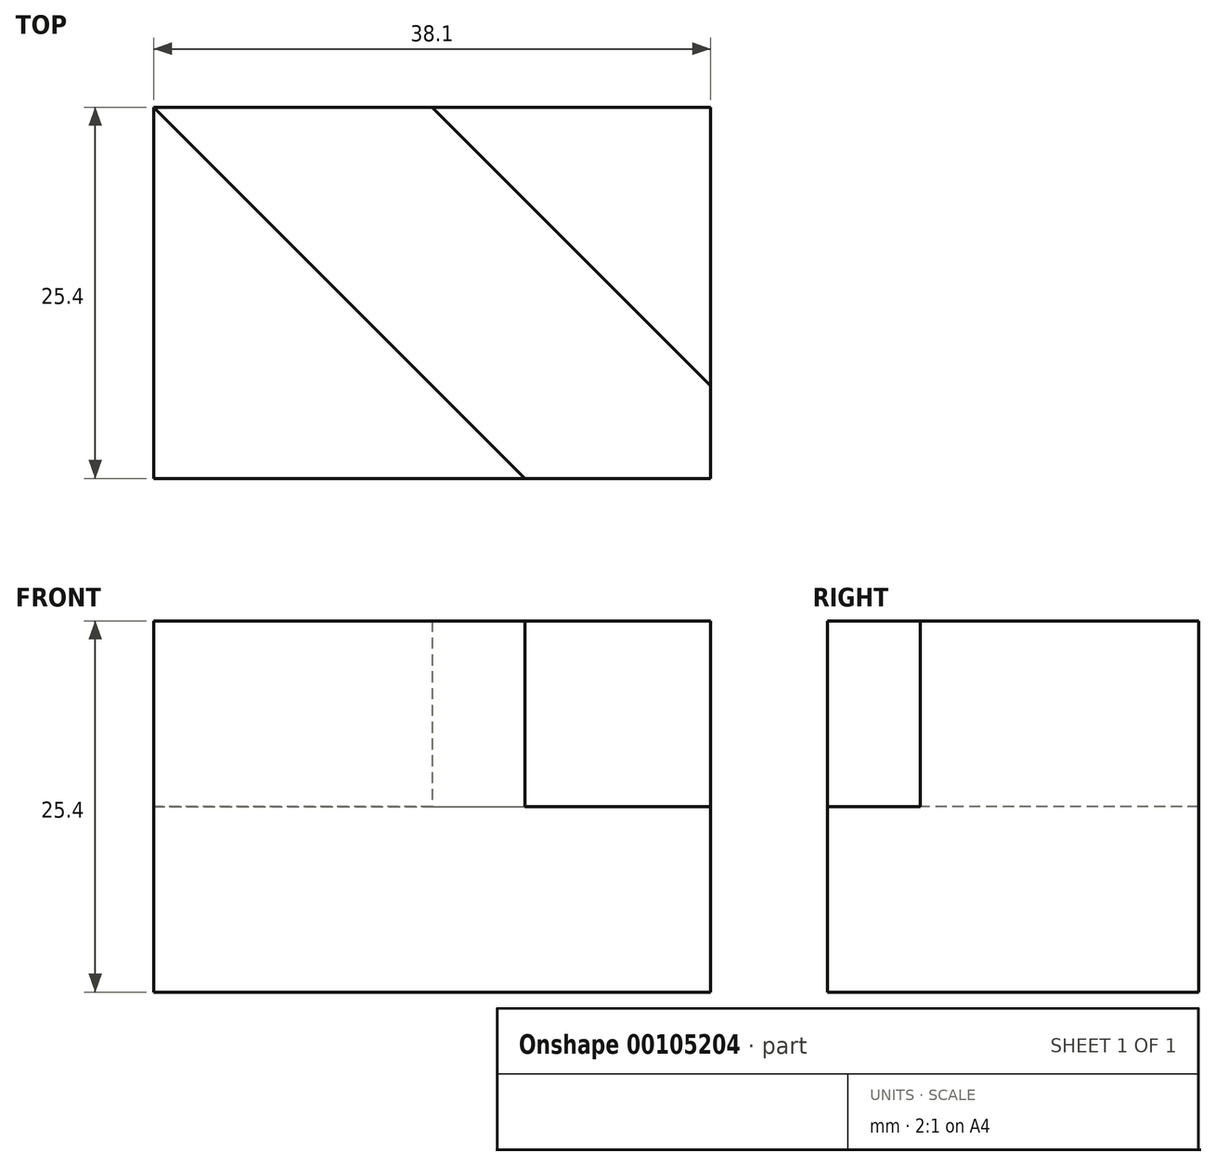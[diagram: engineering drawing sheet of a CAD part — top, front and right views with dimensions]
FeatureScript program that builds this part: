
annotation { "Feature Type Name" : "Feature", "Feature Type Description" : "" }
export const myFeature = defineFeature(function(context is Context, id is Id, definition is map)
    precondition{}
    {
        {
            var Q0;
            Q0=qCreatedBy(makeId("Front.planeOp"),FACE);
            var sketch = newSketch(context, id + "F0", { "sketchPlane" : qUnion([Q0])});
            skLineSegment(sketch, "E0.bottom", {"start": v(0, 0) * mm, "end": v(-38.1, 0) * mm});
            skLineSegment(sketch, "E0.top", {"start": v(0, 25.4) * mm, "end": v(-38.1, 25.4) * mm});
            skLineSegment(sketch, "E0.left", {"start": v(0, 0) * mm, "end": v(0, 25.4) * mm});
            skLineSegment(sketch, "E0.right", {"start": v(-38.1, 0) * mm, "end": v(-38.1, 25.4) * mm});
            skSolve(sketch);
        }
        {
            var Q0;
            Q0 = qSketchRegion(id + "F0", true);
            extrude(context, id + "F1", {"entities" : qUnion([Q0]), "oppositeDirection" : true, "depth" : 25.4 * mm});
        }
        {
            var Q0;
            Q0=qCreatedBy(makeId("Front.planeOp"),FACE);
            var sketch = newSketch(context, id + "F2", { "sketchPlane" : qUnion([Q0])});
            skLineSegment(sketch, "E1.bottom", {"start": v(-12.7, 25.4) * mm, "end": v(0, 25.4) * mm});
            skLineSegment(sketch, "E1.top", {"start": v(-12.7, 12.7) * mm, "end": v(0, 12.7) * mm});
            skLineSegment(sketch, "E1.left", {"start": v(-12.7, 25.4) * mm, "end": v(-12.7, 12.7) * mm});
            skLineSegment(sketch, "E1.right", {"start": v(0, 25.4) * mm, "end": v(0, 12.7) * mm});
            skSolve(sketch);
        }
        {
            var Q0;
            Q0 = qSketchRegion(id + "F2", true);
            extrude(context, id + "F3", {"entities" : qUnion([Q0]), "operationType" : NewBodyOperationType.REMOVE, "oppositeDirection" : true, "depth" : 6.35 * mm});
        }
        {
            var Q0;
            Q0=qCreatedBy(makeId("Top.planeOp"),FACE);
            var sketch = newSketch(context, id + "F4", { "sketchPlane" : qUnion([Q0])});
            skLineSegment(sketch, "E2", {"start": v(-12.7, 0) * mm, "end": v(-38.1, 25.4) * mm});
            skLineSegment(sketch, "E3", {"start": v(-38.1, 25.4) * mm, "end": v(-19.05, 25.4) * mm});
            skLineSegment(sketch, "E4", {"start": v(-19.05, 25.4) * mm, "end": v(0, 6.35) * mm});
            skLineSegment(sketch, "E5", {"start": v(0, 6.35) * mm, "end": v(-12.7, 6.35) * mm});
            skLineSegment(sketch, "E6", {"start": v(-12.7, 6.35) * mm, "end": v(-12.7, 0) * mm});
            skLineSegment(sketch, "E7", {"start": v(-12.7, 0) * mm, "end": v(-12.7, 6.35) * mm});
            skSolve(sketch);
        }
        {
            var Q0;
            Q0 = qSketchRegion(id + "F4", true);
            extrude(context, id + "F5", {"entities" : qUnion([Q0]), "operationType" : NewBodyOperationType.REMOVE, "endBound" : BoundingType.THROUGH_ALL, "depth" : 25.4 * mm});
        }
        {
            var Q0;
            Q0=qCreatedBy(makeId("Front.planeOp"),FACE);
            var sketch = newSketch(context, id + "F6", { "sketchPlane" : qUnion([Q0])});
            skLineSegment(sketch, "E8.bottom", {"start": v(0, 0) * mm, "end": v(-38.1, 0) * mm});
            skLineSegment(sketch, "E8.top", {"start": v(0, 12.7) * mm, "end": v(-38.1, 12.7) * mm});
            skLineSegment(sketch, "E8.left", {"start": v(0, 0) * mm, "end": v(0, 12.7) * mm});
            skLineSegment(sketch, "E8.right", {"start": v(-38.1, 0) * mm, "end": v(-38.1, 12.7) * mm});
            skSolve(sketch);
        }
        {
            var Q0;
            Q0 = qSketchRegion(id + "F6", true);
            extrude(context, id + "F7", {"entities" : qUnion([Q0]), "operationType" : NewBodyOperationType.ADD, "oppositeDirection" : true, "depth" : 25.4 * mm});
        }
    });
